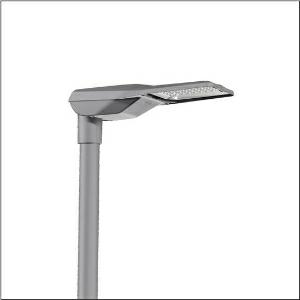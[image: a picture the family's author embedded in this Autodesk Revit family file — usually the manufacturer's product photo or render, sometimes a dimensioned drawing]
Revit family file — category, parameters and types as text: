
# Revit family: streetlight_sl_21_iq_mini___st0_5a_5xe2b41g08hb_4387
name_source: partatom
category: Lighting Fixtures
units: mm (PartAtom-declared; Revit-internal decimal feet)

## family parameters
Cut with Voids When Loaded = No
Host = Face
Light Source = No
Part Type = Normal
Room Calculation Point = No
Round Connector Dimension = Use Diameter
Shared = No

## types (1)
- --- (1 x LED, 9860 lm, 70.9 W, 4000K)
    Apparent Load = 71 VA
    CIE Flux Codes = 41 75 97 100 100
    Color Rendering = 70
    Color Temperature = 4000K
    Default Elevation = 1800 mm
    Description = Streetlight SL 21 iQ mini, mast luminaire, primary light control with lens, of PMMA, primary optical cover: cover, of toughened safety glass, transparent, light distribution: ST0.5a, light emission: direct distribution, primary light characteristic: asymmetric, installation type: post-top, side-entry, LED, High Power LED, rated luminous flux: 9.860lm, luminous efficacy: 139lm/W, light colour: 740, colour temperature: 4000K, control gear: iQ Street-Remote, control: Street-Remote, Auto-Match, Temp-Guard, Lumen-Switch, Night-Set, Smart-Wire, Light-Fading, Desk-Remote (wireless, voltage-free reading and setting of iQ features in the workshop via application-optimized NFC function/RFID function), optimised constant luminous flux control (CLO 2.0), pre-setting: linear dimming characteristic, mains connection: 220..240V, AC, 50/60Hz, start of lifetime: 71W, end of service life: 75W, reduction: 31W, luminaire housing, of diecast aluminium, powder-coated, SITECO metallic grey (DB 702S), corrosivity category C5 high according to DIN EN ISO 12944, please order mast flange separately, inclination adjustable: 0°, 5°, 10°, 15°, sealing non-destructively replaceable, multi-level sealing system, length: 628mm, width: 235mm, height: 110mm, mast flange for spigot size: 42mm (side-entry): 5XC10008XM4, 60/48mm (side-entry/post-top): 5XC10108XM2, 76/60mm (side-entry/post-top): 5XC10108XM1, mounting height: 4..8m, protection rating (complete): IP66, insulation class (complete): insulation class II (safety insulation), certification: CE, ENEC, ENEC+, VDE, impact resistance: IK10, permissible operating ambient temperature for outdoor applications: -40..+50°C, standard-compliant lighting for roads and squares, packaging unit: 1 piece

Light Distribution: ST0.5a
    Height = 110 mm
    Lamp = 1 x LED
    Lamp Light Flux = 9860 lm
    Lamp Power = 70.9 W
    Lamp count = 1
    Length = 625 mm
    Luminous efficacy = 139 lm/W
    Manufacturer = Siteco
    ModVariant = No
    Model = 5XE2B41G08HB
    Number of Poles = 1
    OnlyDefault = Yes
    Power Factor = 1
    Product Name = Streetlight SL 21 iQ mini | ST0.5a
    Product group = mast luminaire | pylon top
    ProductGroupID = 6100
    Protection Class = Protection class II
    Protection Degree = IP 66
    RLX_Detail_Level = 1
    RLX_Emergency_Light_Flux = 0 lm
    RLX_Emergency_Type = 0
    RLX_Emergency_Type_DB = No
    RlxData = <blob elided: 37257 chars, md5=01d50aa5>
    Socket = socket
    Standby Power = 0 W
    System Light Flux = 9860 lm
    System Power = 71 W
    Type Comments = factory setting: luminous flux: 100 % | dim-lin: 254 | 711 mA
    Type Image = l_1003519.jpg
    URL = http://relux.com
    VarID = @adj_157983
    Voltage = 0 V
    Weight = 0.00 kg
    Width = 234 mm

## geometry (parser evidence)
native form markers: Blend x4, Sweep x10
no freeform markers — native parametric forms only
